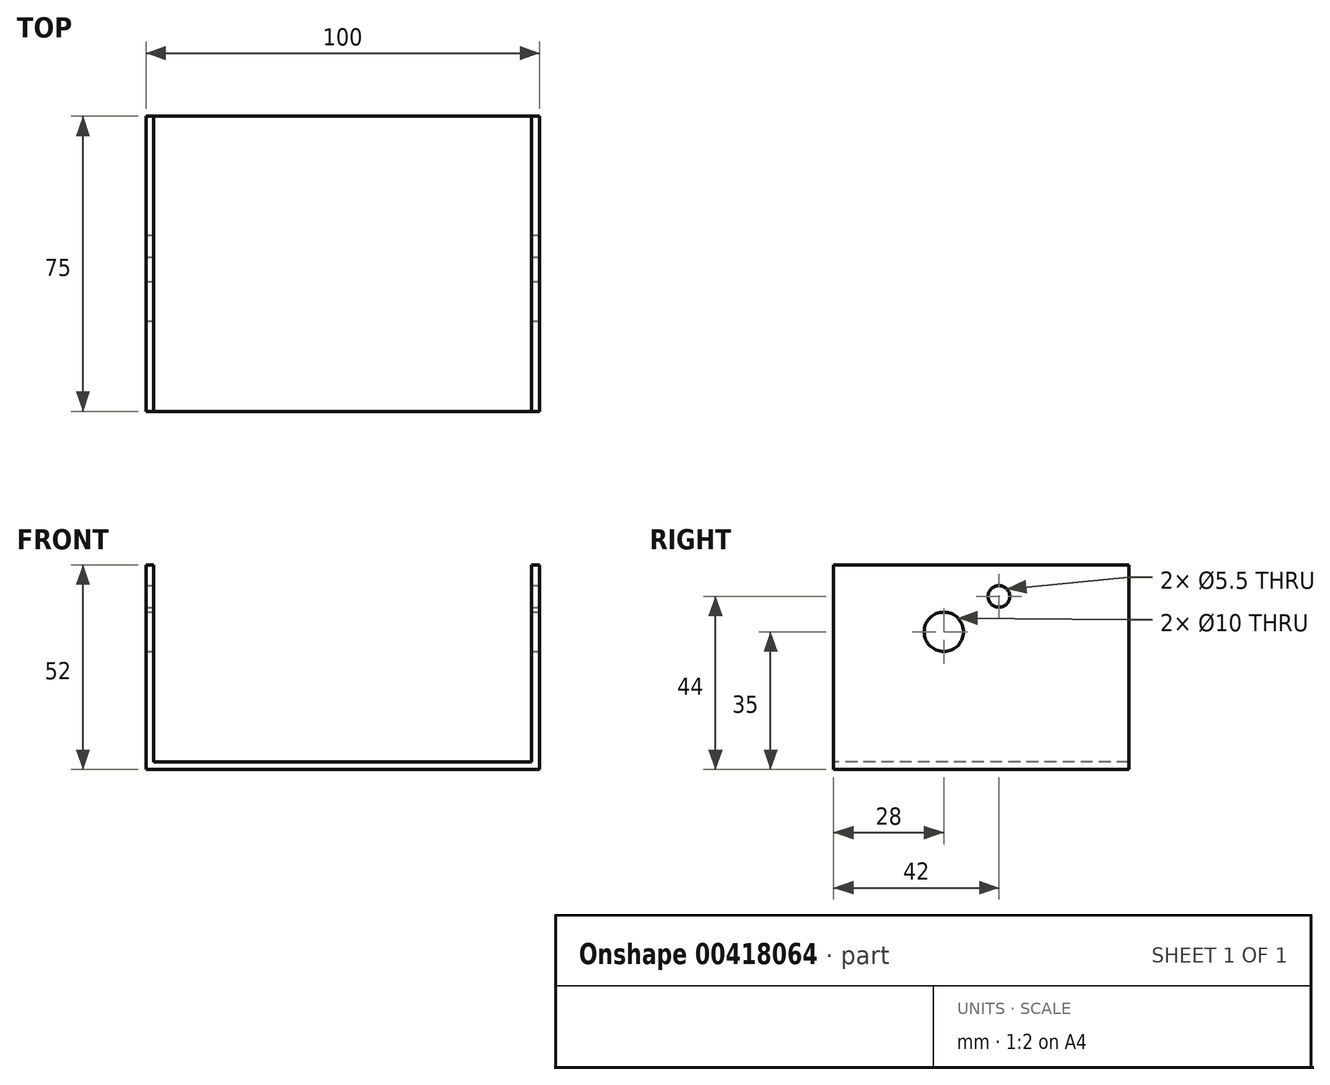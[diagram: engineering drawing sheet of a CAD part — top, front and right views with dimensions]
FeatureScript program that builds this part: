
annotation { "Feature Type Name" : "Feature", "Feature Type Description" : "" }
export const myFeature = defineFeature(function(context is Context, id is Id, definition is map)
    precondition{}
    {
        {
            var Q0;
            Q0=qCreatedBy(makeId("Top.planeOp"),FACE);
            var sketch = newSketch(context, id + "F0", { "sketchPlane" : qUnion([Q0])});
            skLineSegment(sketch, "E0.bottom", {"start": v(0, 0) * mm, "end": v(-100, 0) * mm});
            skLineSegment(sketch, "E0.top", {"start": v(0, 75) * mm, "end": v(-100, 75) * mm});
            skLineSegment(sketch, "E0.left", {"start": v(0, 0) * mm, "end": v(0, 75) * mm});
            skLineSegment(sketch, "E0.right", {"start": v(-100, 0) * mm, "end": v(-100, 75) * mm});
            skSolve(sketch);
        }
        {
            var Q0;
            Q0 = qSketchRegion(id + "F0", true);
            extrude(context, id + "F1", {"entities" : qUnion([Q0]), "depth" : 2 * mm, "offsetDistance" : 25 * mm});
        }
        {
            var Q0;
            Q0=makeQuery(id+"F1.opExtrude","CAP_FACE",FACE,{"disambiguationData":[OSD([sQuery(id+"F0.wireOp",EDGE,"E0.bottom"),sQuery(id+"F0.wireOp",EDGE,"E0.top"),sQuery(id+"F0.wireOp",EDGE,"E0.left"),sQuery(id+"F0.wireOp",EDGE,"E0.right")])],"isStart":false});
            var sketch = newSketch(context, id + "F2", { "sketchPlane" : qUnion([Q0])});
            skLineSegment(sketch, "E1.bottom", {"start": v(-100, 75) * mm, "end": v(-98, 75) * mm});
            skLineSegment(sketch, "E1.top", {"start": v(-100, 0) * mm, "end": v(-98, 0) * mm});
            skLineSegment(sketch, "E1.left", {"start": v(-100, 75) * mm, "end": v(-100, 0) * mm});
            skLineSegment(sketch, "E1.right", {"start": v(-98, 75) * mm, "end": v(-98, 0) * mm});
            skLineSegment(sketch, "E2.bottom", {"start": v(0, 75) * mm, "end": v(-2, 75) * mm});
            skLineSegment(sketch, "E2.top", {"start": v(0, 0) * mm, "end": v(-2, 0) * mm});
            skLineSegment(sketch, "E2.left", {"start": v(0, 75) * mm, "end": v(0, 0) * mm});
            skLineSegment(sketch, "E2.right", {"start": v(-2, 75) * mm, "end": v(-2, 0) * mm});
            skSolve(sketch);
        }
        {
            var Q0;
            Q0 = qSketchRegion(id + "F2", true);
            extrude(context, id + "F3", {"entities" : qUnion([Q0]), "operationType" : NewBodyOperationType.ADD, "depth" : 50 * mm, "offsetDistance" : 25 * mm});
        }
        {
            var Q0;
            Q0=makeQuery(id+"F3.boolean.opBoolean","MERGE",FACE,{"derivedFrom":[makeQuery(id+"F1.opExtrude","SWEPT_FACE",FACE,{"disambiguationData":[OSD([sQuery(id+"F0.wireOp",EDGE,"E0.left")])]}),makeQuery(id+"F3.opExtrude","SWEPT_FACE",FACE,{"disambiguationData":[OSD([sQuery(id+"F2.wireOp",EDGE,"E2.left")])]})]});
            var sketch = newSketch(context, id + "F4", { "sketchPlane" : qUnion([Q0])});
            skCircle(sketch, "E3", {"center": v(28, 35) * mm, "radius": 5 * mm});
            skCircle(sketch, "E4", {"center": v(42, 44) * mm, "radius": 2.75 * mm});
            skSolve(sketch);
        }
        {
            var Q0;
            Q0 = qSketchRegion(id + "F4", true);
            extrude(context, id + "F5", {"entities" : qUnion([Q0]), "operationType" : NewBodyOperationType.REMOVE, "oppositeDirection" : true, "depth" : 100 * mm, "offsetDistance" : 25 * mm});
        }
    });
